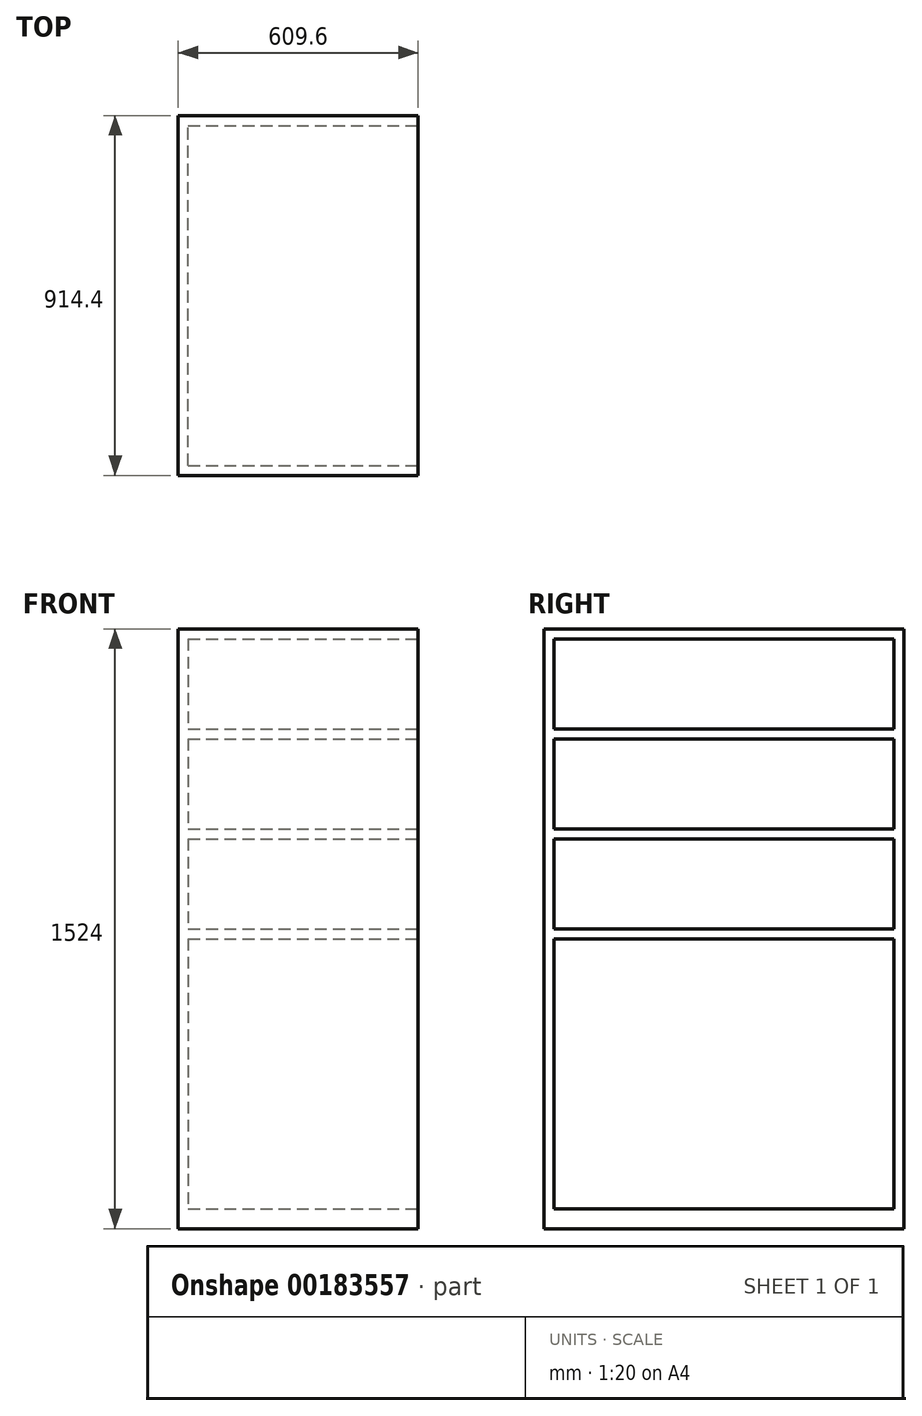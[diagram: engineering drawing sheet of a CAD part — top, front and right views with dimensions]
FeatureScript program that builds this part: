
annotation { "Feature Type Name" : "Feature", "Feature Type Description" : "" }
export const myFeature = defineFeature(function(context is Context, id is Id, definition is map)
    precondition{}
    {
        {
            var Q0;
            Q0=qCreatedBy(makeId("Right.planeOp"),FACE);
            var sketch = newSketch(context, id + "F0", { "sketchPlane" : qUnion([Q0])});
            skLineSegment(sketch, "E0.bottom", {"start": v(457.2, 762) * mm, "end": v(-457.2, 762) * mm});
            skLineSegment(sketch, "E0.top", {"start": v(457.2, -762) * mm, "end": v(-457.2, -762) * mm});
            skLineSegment(sketch, "E0.left", {"start": v(457.2, 762) * mm, "end": v(457.2, -762) * mm});
            skLineSegment(sketch, "E0.right", {"start": v(-457.2, 762) * mm, "end": v(-457.2, -762) * mm});
            skPoint(sketch, "E0.middle", {"position": v(0, 0) * mm});
            skSolve(sketch);
        }
        {
            var Q0;
            Q0=makeQuery(id+"F0.imprint","IMPRINT",FACE,{"disambiguationData":[TD([[makeQuery(id+"F0.imprint","IMPRINT",EDGE,{"derivedFrom":sQuery(id+"F0.wireOp",EDGE,"E0.bottom")}),1.0]])]});
            extrude(context, id + "F1", {"entities" : qUnion([Q0]), "depth" : 609.6 * mm});
        }
        {
            var Q0;
            Q0=makeQuery(id+"F1.opExtrude","CAP_FACE",FACE,{"disambiguationData":[OSD([sQuery(id+"F0.wireOp",EDGE,"E0.bottom"),sQuery(id+"F0.wireOp",EDGE,"E0.top"),sQuery(id+"F0.wireOp",EDGE,"E0.left"),sQuery(id+"F0.wireOp",EDGE,"E0.right")])],"isStart":false});
            var sketch = newSketch(context, id + "F2", { "sketchPlane" : qUnion([Q0])});
            skLineSegment(sketch, "E1.bottom", {"start": v(-431.8, 736.6) * mm, "end": v(431.8, 736.6) * mm});
            skLineSegment(sketch, "E1.top", {"start": v(-431.8, 508) * mm, "end": v(431.8, 508) * mm});
            skLineSegment(sketch, "E1.left", {"start": v(-431.8, 736.6) * mm, "end": v(-431.8, 508) * mm});
            skLineSegment(sketch, "E1.right", {"start": v(431.8, 736.6) * mm, "end": v(431.8, 508) * mm});
            skLineSegment(sketch, "E2.0.1.0", {"start": v(-431.8, 482.6) * mm, "end": v(431.8, 482.6) * mm});
            skLineSegment(sketch, "E2.0.1.1", {"start": v(-431.8, 254) * mm, "end": v(431.8, 254) * mm});
            skLineSegment(sketch, "E2.0.1.2", {"start": v(-431.8, 482.6) * mm, "end": v(-431.8, 254) * mm});
            skLineSegment(sketch, "E2.0.1.3", {"start": v(431.8, 482.6) * mm, "end": v(431.8, 254) * mm});
            skLineSegment(sketch, "E2.0.2.0", {"start": v(-431.8, 228.6) * mm, "end": v(431.8, 228.6) * mm});
            skLineSegment(sketch, "E2.0.2.1", {"start": v(-431.8, 0) * mm, "end": v(431.8, 0) * mm});
            skLineSegment(sketch, "E2.0.2.2", {"start": v(-431.8, 228.6) * mm, "end": v(-431.8, 0) * mm});
            skLineSegment(sketch, "E2.0.2.3", {"start": v(431.8, 228.6) * mm, "end": v(431.8, 0) * mm});
            skLineSegment(sketch, "E2.direction1", {"start": v(-431.8, 736.6) * mm, "end": v(-403.86, 736.6) * mm, "construction": true});
            skLineSegment(sketch, "E2.direction2", {"start": v(-431.8, 736.6) * mm, "end": v(-431.8, 482.6) * mm, "construction": true});
            skSolve(sketch);
        }
        {
            var Q0;
            Q0 = qSketchRegion(id + "F2", true);
            extrude(context, id + "F3", {"entities" : qUnion([Q0]), "operationType" : NewBodyOperationType.REMOVE, "oppositeDirection" : true, "depth" : 584.2 * mm});
        }
        {
            var Q0;
            Q0=makeQuery(id+"F1.opExtrude","CAP_FACE",FACE,{"disambiguationData":[OSD([sQuery(id+"F0.wireOp",EDGE,"E0.bottom"),sQuery(id+"F0.wireOp",EDGE,"E0.top"),sQuery(id+"F0.wireOp",EDGE,"E0.left"),sQuery(id+"F0.wireOp",EDGE,"E0.right")])],"isStart":false});
            var sketch = newSketch(context, id + "F4", { "sketchPlane" : qUnion([Q0])});
            skLineSegment(sketch, "E3.bottom", {"start": v(-431.8, -25.4) * mm, "end": v(431.8, -25.4) * mm});
            skLineSegment(sketch, "E3.top", {"start": v(-431.8, -711.2) * mm, "end": v(431.8, -711.2) * mm});
            skLineSegment(sketch, "E3.left", {"start": v(-431.8, -25.4) * mm, "end": v(-431.8, -711.2) * mm});
            skLineSegment(sketch, "E3.right", {"start": v(431.8, -25.4) * mm, "end": v(431.8, -711.2) * mm});
            skSolve(sketch);
        }
        {
            var Q0;
            Q0 = qSketchRegion(id + "F4", true);
            extrude(context, id + "F5", {"entities" : qUnion([Q0]), "operationType" : NewBodyOperationType.REMOVE, "oppositeDirection" : true, "depth" : 584.2 * mm});
        }
    });
